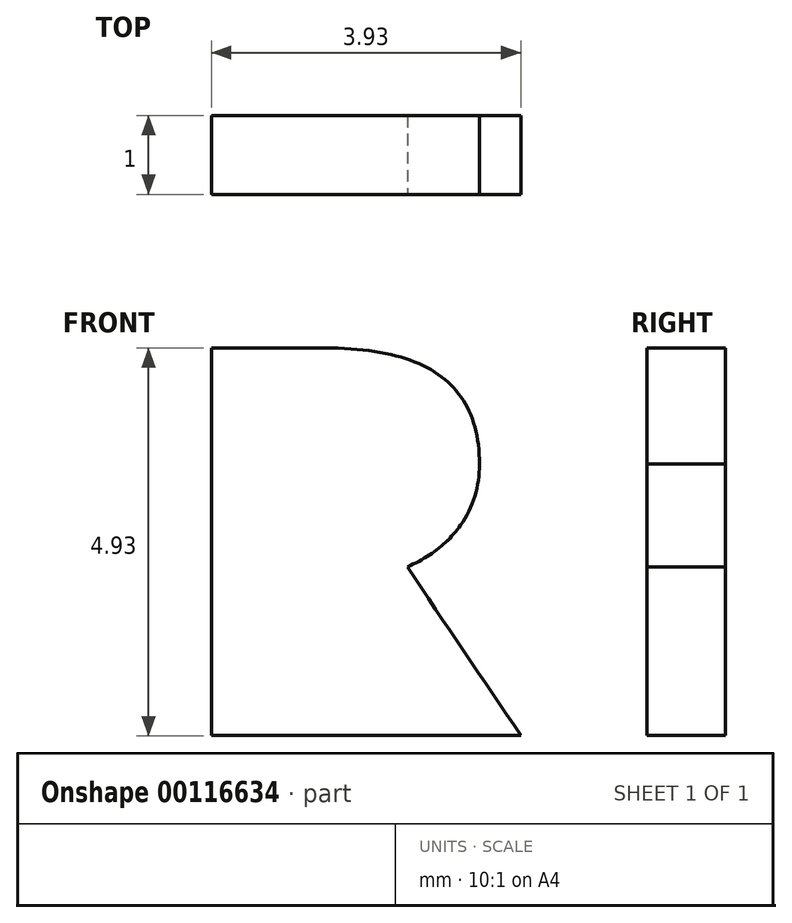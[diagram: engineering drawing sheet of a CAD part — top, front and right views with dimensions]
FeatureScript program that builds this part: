
annotation { "Feature Type Name" : "Feature", "Feature Type Description" : "" }
export const myFeature = defineFeature(function(context is Context, id is Id, definition is map)
    precondition{}
    {
        {
            var Q0;
            Q0=qCreatedBy(makeId("Front.planeOp"),FACE);
            var sketch = newSketch(context, id + "F0", { "sketchPlane" : qUnion([Q0])});
            skLineSegment(sketch, "E0", {"start": v(0, 3.96) * mm, "end": v(0, 0.17) * mm, "construction": true});
            skLineSegment(sketch, "E1", {"start": v(-5.17, 0) * mm, "end": v(4.3, 0) * mm, "construction": true});
            skText(sketch, "E2", { "text": "R", "fontName": "OpenSans-Bold.ttf"});
            skLineSegment(sketch, "E3.bottom", {"start": v(-3.6, 3.96) * mm, "end": v(3.6, 3.96) * mm});
            skLineSegment(sketch, "E3.top", {"start": v(-3.6, -3.96) * mm, "end": v(3.6, -3.96) * mm});
            skLineSegment(sketch, "E3.left", {"start": v(-3.6, 3.96) * mm, "end": v(-3.6, -3.96) * mm});
            skLineSegment(sketch, "E3.right", {"start": v(3.6, 3.96) * mm, "end": v(3.6, -3.96) * mm});
            skPoint(sketch, "E4", {"position": v(-3.6, 0) * mm});
            skLineSegment(sketch, "E5", {"start": v(-2.5, -2.76) * mm, "end": v(2.5, -2.76) * mm});
            const initialGuessF0  = {"E2": [-0.0025, -0.00276, 1, 0, 0.00497]};
            skSetInitialGuess(sketch, initialGuessF0);
            skSolve(sketch);
        }
        {
            var Q0;
            Q0=makeQuery(id+"F0.imprint","IMPRINT",FACE,{"disambiguationData":[TD([[makeQuery(id+"F0.imprint","IMPRINT",EDGE,{"derivedFrom":sQuery(id+"F0.wireOp",EDGE,"E2.sketch_text.stroke-0")}),-1.0]])]});
            var Q1;
            Q1=makeQuery(id+"F0.imprint","IMPRINT",FACE,{"disambiguationData":[TD([[makeQuery(id+"F0.imprint","IMPRINT",EDGE,{"derivedFrom":sQuery(id+"F0.wireOp",EDGE,"E2.sketch_text.stroke-0")}),1.0]])]});
            var Q2;
            {var subQ0=sQuery(id+"F0.wireOp",EDGE,"E2.sketch_text.stroke-7");Q2=makeQuery(id+"F0.imprint","IMPRINT",FACE,{"disambiguationData":[TD([[makeQuery(id+"F0.imprint","IMPRINT",EDGE,{"derivedFrom":subQ0}),1.0]])]});}
            extrude(context, id + "F1", {"entities" : qUnion([Q0, Q1, Q2]), "oppositeDirection" : true, "depth" : 1 * mm});
        }
    });
